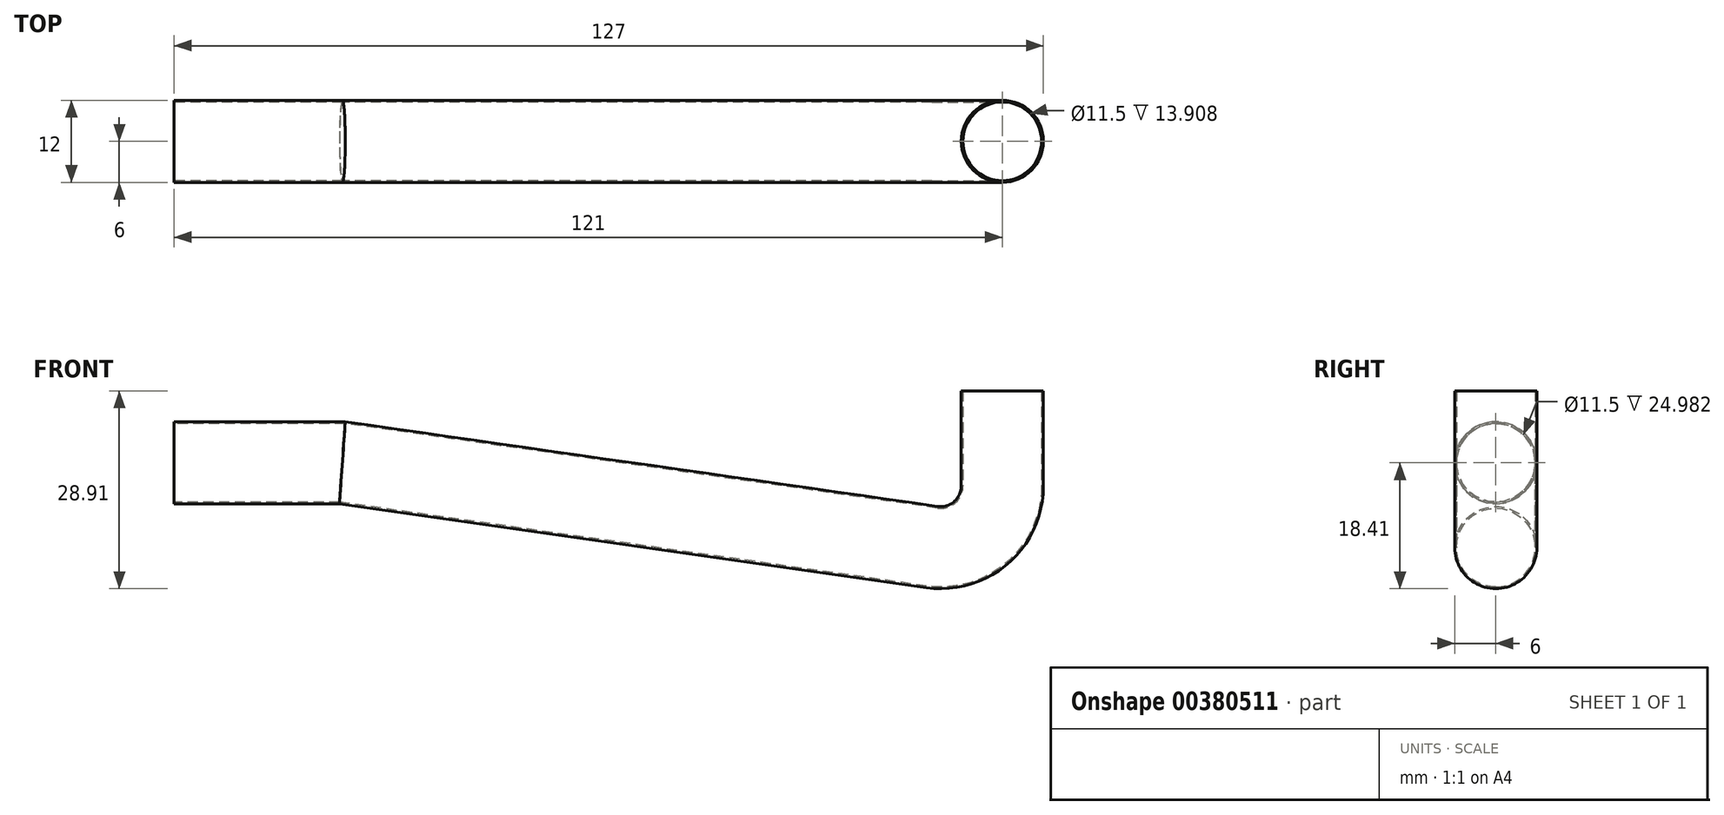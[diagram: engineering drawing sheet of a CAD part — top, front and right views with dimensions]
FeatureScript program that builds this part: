
annotation { "Feature Type Name" : "Feature", "Feature Type Description" : "" }
export const myFeature = defineFeature(function(context is Context, id is Id, definition is map)
    precondition{}
    {
        {
            var Q0;
            Q0=qCreatedBy(makeId("Top.planeOp"),FACE);
            var sketch = newSketch(context, id + "F0", { "sketchPlane" : qUnion([Q0])});
            skCircle(sketch, "E0", {"center": v(0, 0) * mm, "radius": 6 * mm});
            skCircle(sketch, "E1", {"center": v(0, 0) * mm, "radius": 5.75 * mm});
            skSolve(sketch);
        }
        {
            var Q0;
            Q0=qCreatedBy(makeId("Front.planeOp"),FACE);
            var sketch = newSketch(context, id + "F1", { "sketchPlane" : qUnion([Q0])});
            skLineSegment(sketch, "E2", {"start": v(-121, 0) * mm, "end": v(0, 0) * mm});
            skLineSegment(sketch, "E3", {"start": v(-121, -10.5) * mm, "end": v(-96.71, -10.5) * mm});
            skLineSegment(sketch, "E4", {"start": v(-95.3, -10.6) * mm, "end": v(-9.13, -22.92) * mm});
            skPoint(sketch, "E5.visualSharp", {"position": v(-96, -10.5) * mm});
            skArc(sketch, "E5.filletArc", {"start": v(-95.3, -10.6) * mm, "mid": v(-96, -10.53) * mm, "end": v(-96.71, -10.5) * mm});
            skLineSegment(sketch, "E6", {"start": v(0, -15) * mm, "end": v(0, 0) * mm});
            skPoint(sketch, "E7.visualSharp", {"position": v(0, 0) * mm});
            skArc(sketch, "E7.filletArc", {"start": v(-9.13, -22.92) * mm, "mid": v(-2.76, -21.04) * mm, "end": v(0, -15) * mm});
            skLineSegment(sketch, "E8", {"start": v(0, 0) * mm, "end": v(-6, 0) * mm});
            skLineSegment(sketch, "E9", {"start": v(-121, -4.5) * mm, "end": v(-121, -16.5) * mm});
            skLineSegment(sketch, "E10", {"start": v(-121, -4.5) * mm, "end": v(-96, -4.5) * mm});
            skLineSegment(sketch, "E11", {"start": v(-121, -16.5) * mm, "end": v(-96.71, -16.5) * mm});
            skLineSegment(sketch, "E12", {"start": v(-95.3, -16.6) * mm, "end": v(-7.7, -29.12) * mm});
            skLineSegment(sketch, "E13", {"start": v(-96, -4.5) * mm, "end": v(-9.42, -16.88) * mm});
            skLineSegment(sketch, "E14", {"start": v(-6, -13.9) * mm, "end": v(-6, 0) * mm});
            skLineSegment(sketch, "E15", {"start": v(6, -17.25) * mm, "end": v(6, 0) * mm});
            skLineSegment(sketch, "E16", {"start": v(6, 0) * mm, "end": v(-6, 0) * mm});
            skPoint(sketch, "E17.visualSharp", {"position": v(-6, -17.37) * mm});
            skArc(sketch, "E17.filletArc", {"start": v(-9.42, -16.88) * mm, "mid": v(-7.03, -16.17) * mm, "end": v(-6, -13.9) * mm});
            skPoint(sketch, "E18.visualSharp", {"position": v(6, -31.08) * mm});
            skArc(sketch, "E18.filletArc", {"start": v(-7.7, -29.12) * mm, "mid": v(1.86, -26.31) * mm, "end": v(6, -17.25) * mm});
            skPoint(sketch, "E19.visualSharp", {"position": v(-96, -16.5) * mm});
            skArc(sketch, "E19.filletArc", {"start": v(-95.3, -16.6) * mm, "mid": v(-96, -16.53) * mm, "end": v(-96.71, -16.5) * mm});
            skSolve(sketch);
        }
        {
            var Q0;
            Q0=makeQuery(id+"F0.imprint","IMPRINT",FACE,{"disambiguationData":[TD([[makeQuery(id+"F0.imprint","IMPRINT",EDGE,{"derivedFrom":sQuery(id+"F0.wireOp",EDGE,"E0")}),1.0]])]});
            var Q1;
            Q1=sQuery(id+"F1.wireOp",EDGE,"E14");
            var Q2;
            Q2=sQuery(id+"F1.wireOp",EDGE,"E17.filletArc");
            var Q3;
            Q3=sQuery(id+"F1.wireOp",EDGE,"E13");
            var Q4;
            Q4=sQuery(id+"F1.wireOp",EDGE,"E10");
            sweep(context, id + "F2", {"profiles" : qUnion([Q0]), "path" : qUnion([Q1, Q2, Q3, Q4])});
        }
    });
